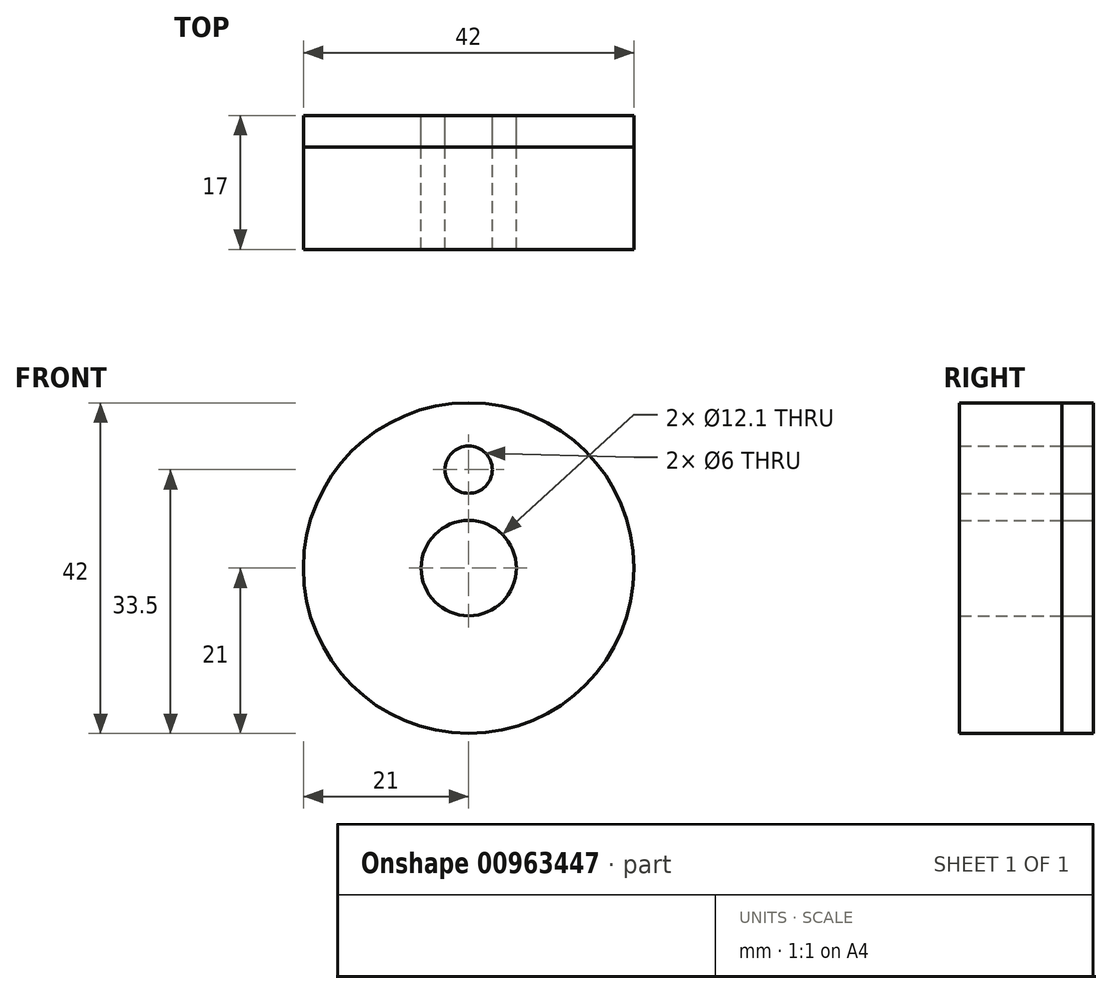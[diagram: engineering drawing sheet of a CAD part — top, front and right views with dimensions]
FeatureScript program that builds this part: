
annotation { "Feature Type Name" : "Feature", "Feature Type Description" : "" }
export const myFeature = defineFeature(function(context is Context, id is Id, definition is map)
    precondition{}
    {
        {
            var Q0;
            Q0=qCreatedBy(makeId("Front.planeOp"),FACE);
            var sketch = newSketch(context, id + "F0", { "sketchPlane" : qUnion([Q0])});
            skCircle(sketch, "E0", {"center": v(0, 0) * mm, "radius": 21 * mm});
            skCircle(sketch, "E1", {"center": v(0, 0) * mm, "radius": 6.05 * mm});
            skPoint(sketch, "E2", {"position": v(0, 12.5) * mm});
            skCircle(sketch, "E3", {"center": v(0, 12.5) * mm, "radius": 3 * mm});
            skSolve(sketch);
        }
        {
            var Q0;
            Q0=makeQuery(id+"F0.imprint","IMPRINT",FACE,{"disambiguationData":[TD([[makeQuery(id+"F0.imprint","IMPRINT",EDGE,{"derivedFrom":sQuery(id+"F0.wireOp",EDGE,"E0")}),1.0]])]});
            extrude(context, id + "F1", {"entities" : qUnion([Q0]), "depth" : 17 * mm});
        }
        {
            var Q0;
            Q0=qSketchRegion(id+"F0",true);
            extrude(context, id + "F2", {"entities" : qUnion([Q0]), "depth" : 4 * mm});
        }
    });
